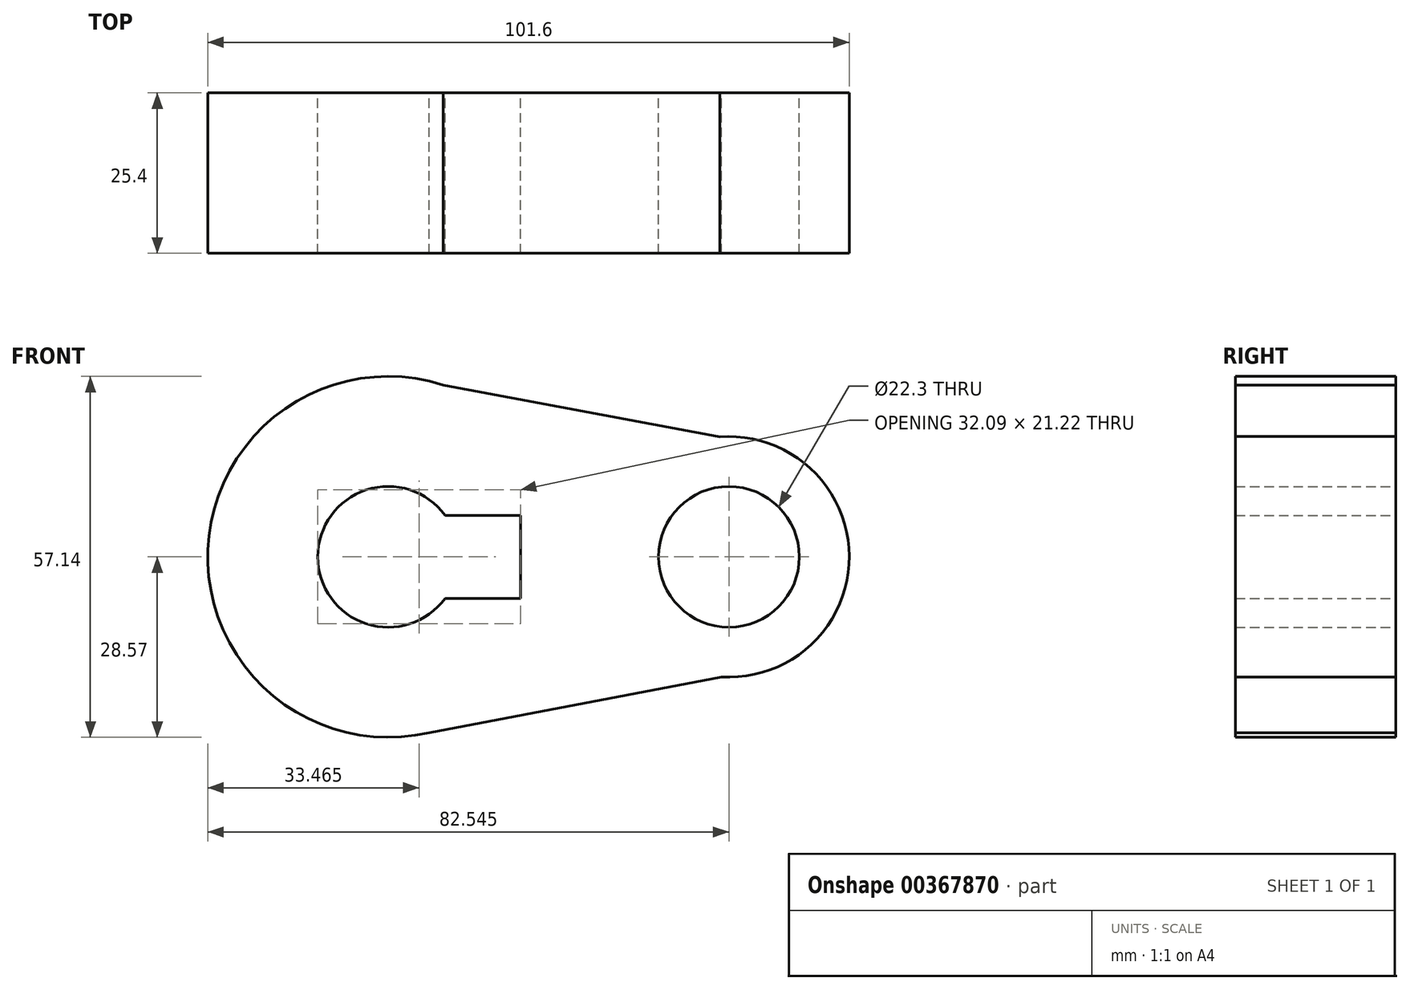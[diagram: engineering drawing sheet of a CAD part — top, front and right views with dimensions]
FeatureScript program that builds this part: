
annotation { "Feature Type Name" : "Feature", "Feature Type Description" : "" }
export const myFeature = defineFeature(function(context is Context, id is Id, definition is map)
    precondition{}
    {
        {
            var Q0;
            Q0=qCreatedBy(makeId("Front.planeOp"),FACE);
            var sketch = newSketch(context, id + "F0", { "sketchPlane" : qUnion([Q0])});
            skCircle(sketch, "E0", {"center": v(0, 0) * mm, "radius": 28.58 * mm});
            skCircle(sketch, "E1", {"center": v(53.98, 0) * mm, "radius": 19.05 * mm});
            skLineSegment(sketch, "E2", {"start": v(8.7, 27.22) * mm, "end": v(52.52, 19) * mm});
            skLineSegment(sketch, "E3", {"start": v(6.47, -27.83) * mm, "end": v(52.77, -19.01) * mm});
            skCircle(sketch, "E4", {"center": v(0, 0) * mm, "radius": 11.15 * mm});
            skCircle(sketch, "E5", {"center": v(53.98, 0) * mm, "radius": 11.15 * mm});
            skLineSegment(sketch, "E6.bottom", {"start": v(-20.94, 6.57) * mm, "end": v(20.94, 6.57) * mm});
            skLineSegment(sketch, "E6.top", {"start": v(-20.94, -6.57) * mm, "end": v(20.94, -6.57) * mm});
            skLineSegment(sketch, "E6.left", {"start": v(-20.94, 6.57) * mm, "end": v(-20.94, -6.57) * mm});
            skLineSegment(sketch, "E6.right", {"start": v(20.94, 6.57) * mm, "end": v(20.94, -6.57) * mm});
            skSolve(sketch);
        }
        {
            var Q0;
            {var subQ7=sQuery(id+"F0.wireOp",EDGE,"E6.left");Q0=makeQuery(id+"F0.imprint","IMPRINT",FACE,{"disambiguationData":[TD([[makeQuery(id+"F0.imprint","IMPRINT",EDGE,{"derivedFrom":subQ7}),-1.0]])]});}
            var Q1;
            {var subQ5=sQuery(id+"F0.wireOp",EDGE,"E6.left");Q1=makeQuery(id+"F0.imprint","IMPRINT",FACE,{"disambiguationData":[TD([[makeQuery(id+"F0.imprint","IMPRINT",EDGE,{"derivedFrom":subQ5}),1.0]])]});}
            var Q2;
            {var subQ0=sQuery(id+"F0.wireOp",EDGE,"E2");Q2=makeQuery(id+"F0.imprint","IMPRINT",FACE,{"disambiguationData":[TD([[makeQuery(id+"F0.imprint","IMPRINT",EDGE,{"derivedFrom":subQ0}),-1.0]])]});}
            var Q3;
            Q3=makeQuery(id+"F0.imprint","IMPRINT",FACE,{"disambiguationData":[TD([[makeQuery(id+"F0.imprint","IMPRINT",EDGE,{"derivedFrom":sQuery(id+"F0.wireOp",EDGE,"E5")}),-1.0]])]});
            extrude(context, id + "F1", {"entities" : qUnion([Q0, Q1, Q2, Q3]), "depth" : 25.4 * mm});
        }
    });
